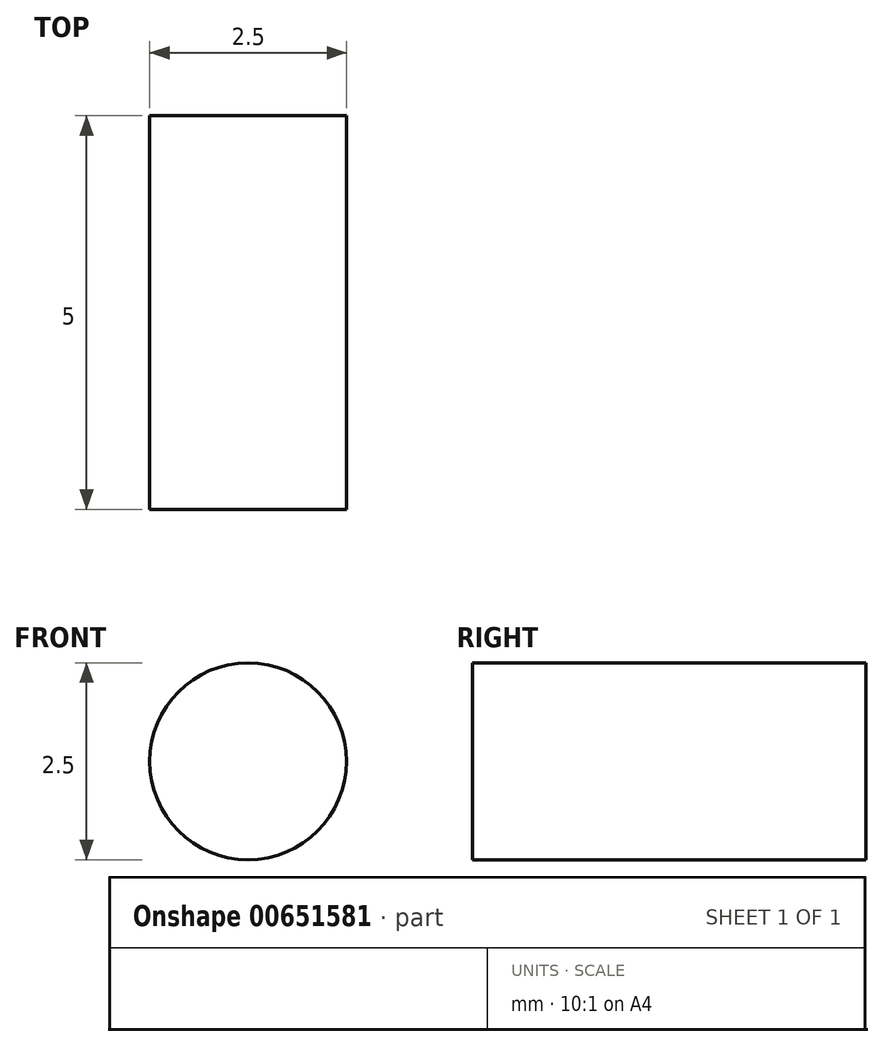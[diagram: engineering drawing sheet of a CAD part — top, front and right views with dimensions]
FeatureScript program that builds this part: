
annotation { "Feature Type Name" : "Feature", "Feature Type Description" : "" }
export const myFeature = defineFeature(function(context is Context, id is Id, definition is map)
    precondition{}
    {
        {
            var Q0;
            Q0=qCreatedBy(makeId("Front.planeOp"),FACE);
            var sketch = newSketch(context, id + "F0", { "sketchPlane" : qUnion([Q0])});
            skCircle(sketch, "E0", {"center": v(0, 0) * mm, "radius": 1.25 * mm});
            skSolve(sketch);
        }
        {
            var Q0;
            Q0=makeQuery(id+"F0.imprint","IMPRINT",FACE,{"disambiguationData":[TD([[makeQuery(id+"F0.imprint","IMPRINT",EDGE,{"derivedFrom":sQuery(id+"F0.wireOp",EDGE,"E0")}),1.0]])]});
            extrude(context, id + "F1", {"entities" : qUnion([Q0]), "depth" : 5 * mm});
        }
    });
